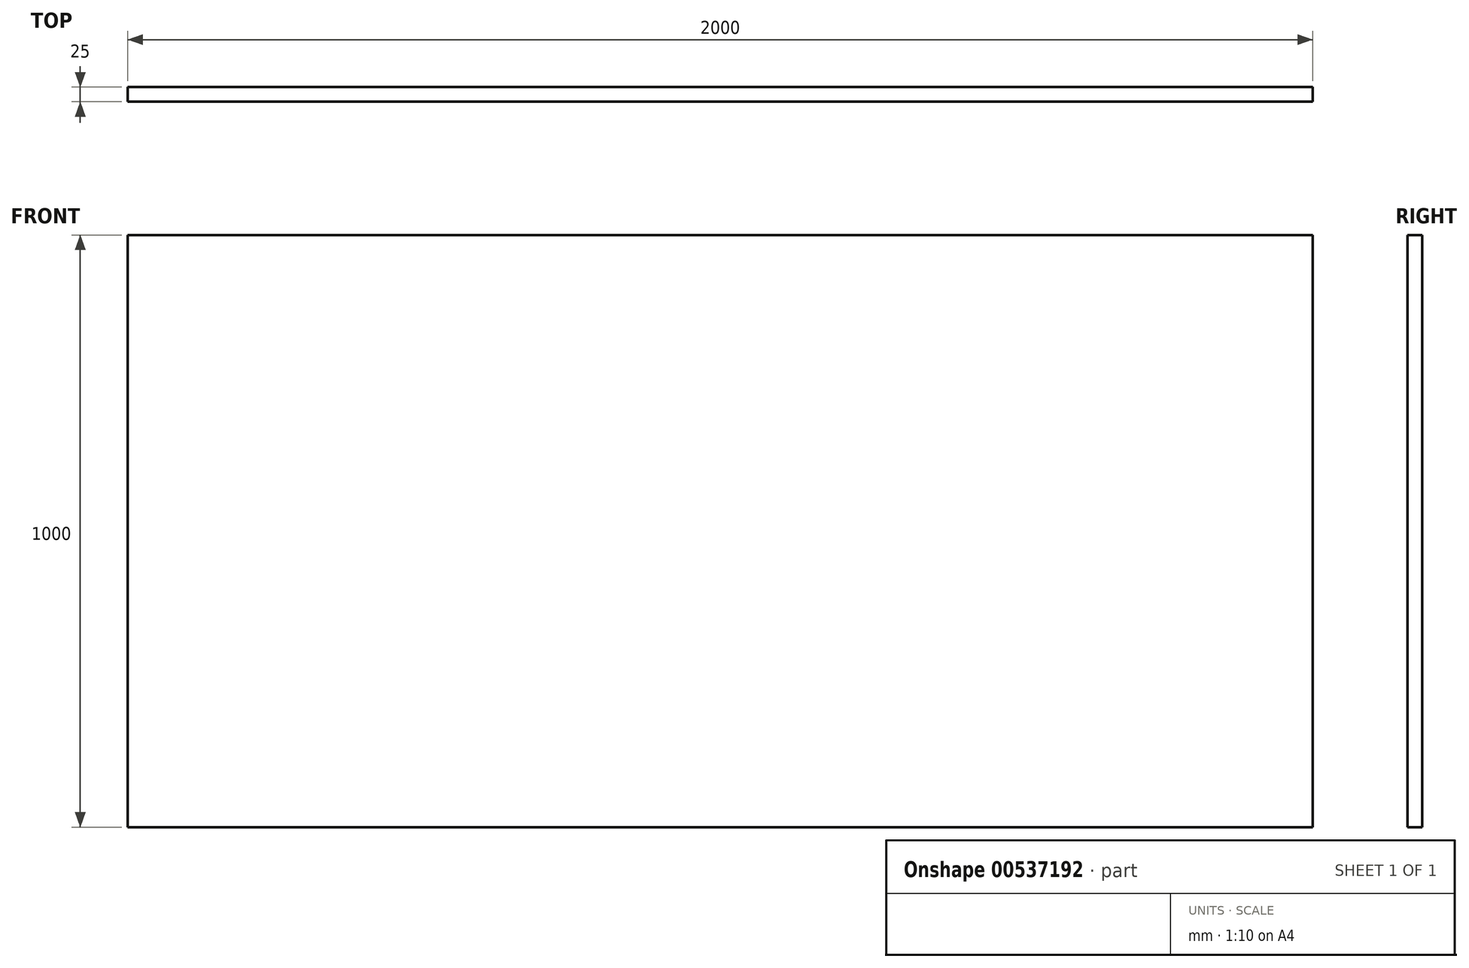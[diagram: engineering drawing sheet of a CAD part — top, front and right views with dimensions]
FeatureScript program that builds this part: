
annotation { "Feature Type Name" : "Feature", "Feature Type Description" : "" }
export const myFeature = defineFeature(function(context is Context, id is Id, definition is map)
    precondition{}
    {
        {
            var Q0;
            Q0=qCreatedBy(makeId("Front.planeOp"),FACE);
            var sketch = newSketch(context, id + "F0", { "sketchPlane" : qUnion([Q0])});
            skLineSegment(sketch, "E0.bottom", {"start": v(1000, 500) * mm, "end": v(-1000, 500) * mm});
            skLineSegment(sketch, "E0.top", {"start": v(1000, -500) * mm, "end": v(-1000, -500) * mm});
            skLineSegment(sketch, "E0.left", {"start": v(1000, 500) * mm, "end": v(1000, -500) * mm});
            skLineSegment(sketch, "E0.right", {"start": v(-1000, 500) * mm, "end": v(-1000, -500) * mm});
            skPoint(sketch, "E0.middle", {"position": v(0, 0) * mm});
            skSolve(sketch);
        }
        {
            var Q0;
            Q0=makeQuery(id+"F0.imprint","IMPRINT",FACE,{"disambiguationData":[TD([[makeQuery(id+"F0.imprint","IMPRINT",EDGE,{"derivedFrom":sQuery(id+"F0.wireOp",EDGE,"E0.bottom")}),1.0]])]});
            extrude(context, id + "F1", {"entities" : qUnion([Q0]), "depth" : 25 * mm, "offsetDistance" : 25 * mm});
        }
    });
